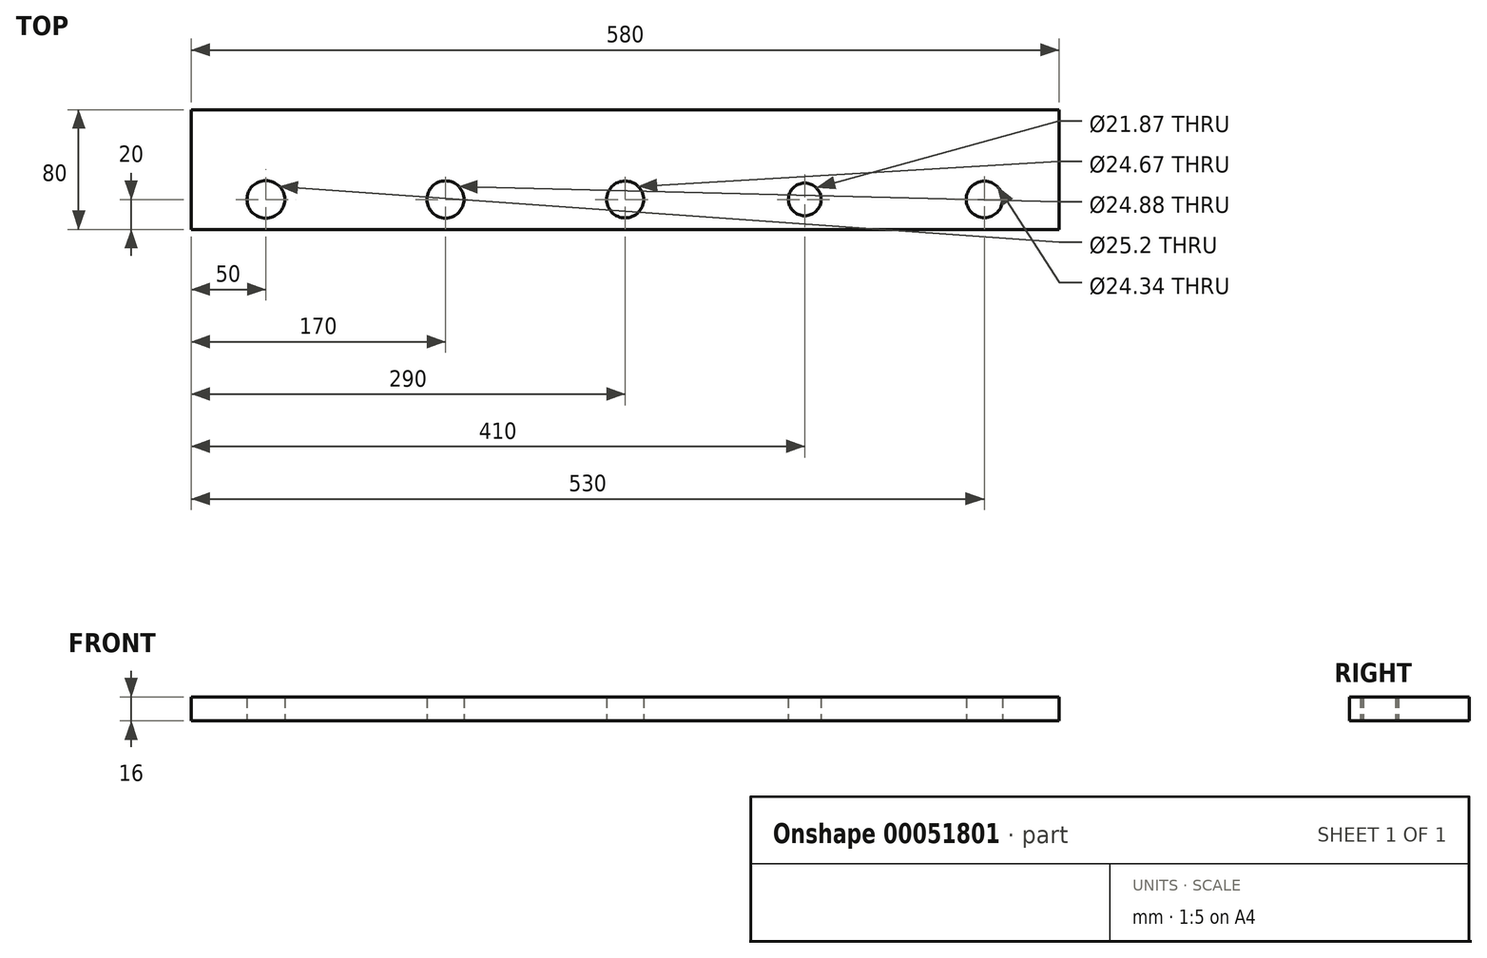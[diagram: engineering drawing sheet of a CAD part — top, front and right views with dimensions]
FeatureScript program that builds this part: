
annotation { "Feature Type Name" : "Feature", "Feature Type Description" : "" }
export const myFeature = defineFeature(function(context is Context, id is Id, definition is map)
    precondition{}
    {
        {
            var Q0;
            Q0=qCreatedBy(makeId("Top.planeOp"),FACE);
            var sketch = newSketch(context, id + "F0", { "sketchPlane" : qUnion([Q0])});
            skLineSegment(sketch, "E0.rect.bottom", {"start": v(290, 40) * mm, "end": v(-290, 40) * mm});
            skLineSegment(sketch, "E0.rect.top", {"start": v(290, -40) * mm, "end": v(-290, -40) * mm});
            skLineSegment(sketch, "E0.rect.left", {"start": v(290, 40) * mm, "end": v(290, -40) * mm});
            skLineSegment(sketch, "E0.rect.right", {"start": v(-290, 40) * mm, "end": v(-290, -40) * mm});
            skPoint(sketch, "E0.rect.middle", {"position": v(0, 0) * mm});
            skLineSegment(sketch, "E1", {"start": v(-290, -20) * mm, "end": v(290, -20) * mm, "construction": true});
            skLineSegment(sketch, "E2", {"start": v(-240, -40) * mm, "end": v(-240, 40) * mm, "construction": true});
            skLineSegment(sketch, "E3", {"start": v(-120, -40) * mm, "end": v(-120, 40) * mm, "construction": true});
            skCircle(sketch, "E4", {"center": v(-240, -20) * mm, "radius": 12.6 * mm});
            skCircle(sketch, "E5", {"center": v(-120, -20) * mm, "radius": 12.44 * mm});
            skLineSegment(sketch, "E6", {"start": v(0, 40) * mm, "end": v(0, -40) * mm, "construction": true});
            skLineSegment(sketch, "E7", {"start": v(120, 40) * mm, "end": v(120, -40) * mm, "construction": true});
            skLineSegment(sketch, "E8", {"start": v(240, 40) * mm, "end": v(240, -40) * mm, "construction": true});
            skCircle(sketch, "E9", {"center": v(0, -20) * mm, "radius": 12.34 * mm});
            skCircle(sketch, "E10", {"center": v(120, -20) * mm, "radius": 10.94 * mm});
            skCircle(sketch, "E11", {"center": v(240, -20) * mm, "radius": 12.17 * mm});
            skSolve(sketch);
        }
        {
            var Q0;
            Q0 = qSketchRegion(id + "F0", true);
            extrude(context, id + "F1", {"entities" : qUnion([Q0]), "depth" : 16 * mm});
        }
    });
